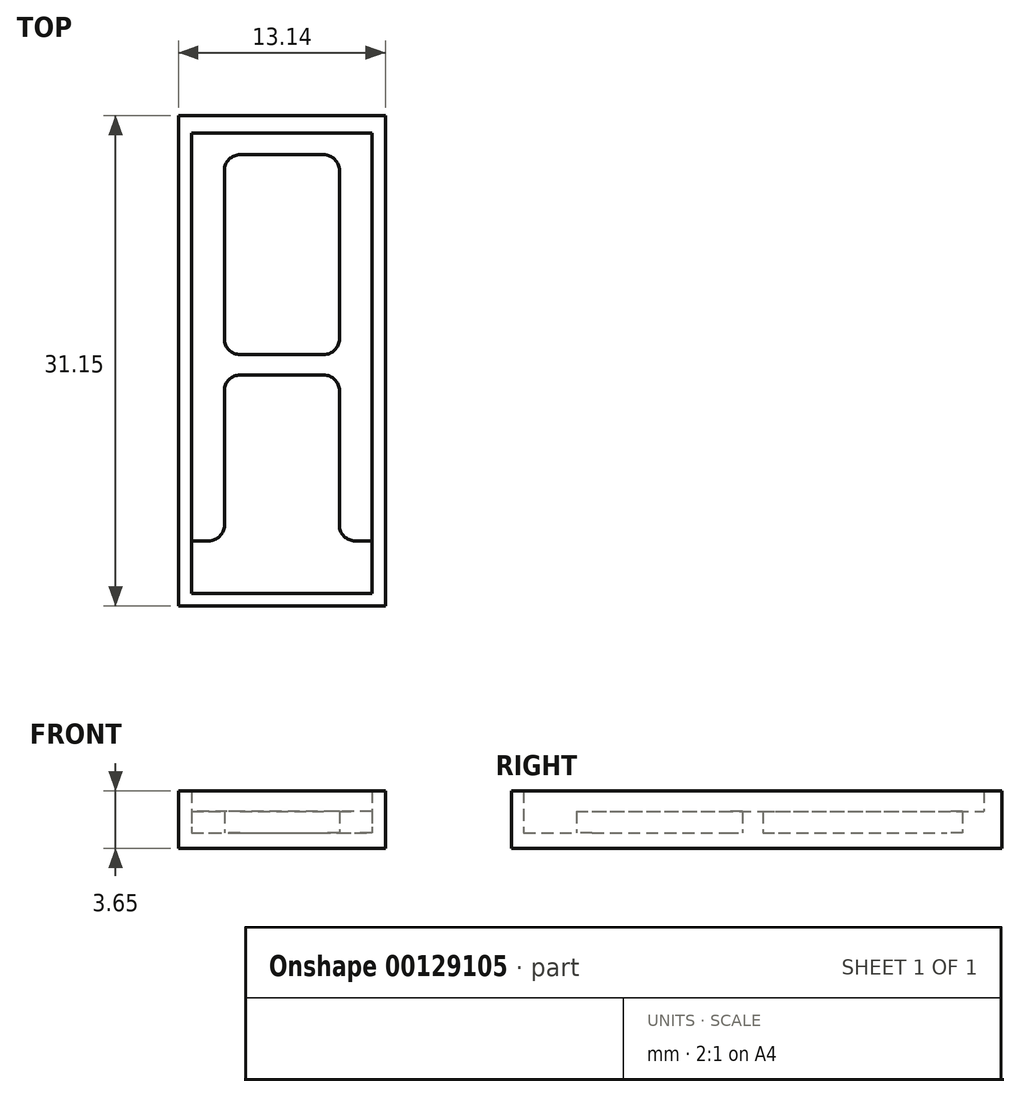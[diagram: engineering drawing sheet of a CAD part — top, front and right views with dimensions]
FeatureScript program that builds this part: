
annotation { "Feature Type Name" : "Feature", "Feature Type Description" : "" }
export const myFeature = defineFeature(function(context is Context, id is Id, definition is map)
    precondition{}
    {
        {
            var Q0;
            Q0=qCreatedBy(makeId("Top.planeOp"),FACE);
            var sketch = newSketch(context, id + "F0", { "sketchPlane" : qUnion([Q0])});
            skLineSegment(sketch, "E0", {"start": v(5.72, 5.55) * mm, "end": v(5.72, 34.8) * mm});
            skLineSegment(sketch, "E1", {"start": v(5.72, 8.9) * mm, "end": v(4.65, 8.9) * mm});
            skLineSegment(sketch, "E2", {"start": v(3.65, 9.9) * mm, "end": v(3.65, 18.44) * mm});
            skLineSegment(sketch, "E3", {"start": v(6.57, 35.92) * mm, "end": v(6.57, 4.77) * mm});
            skLineSegment(sketch, "E4", {"start": v(0, 0) * mm, "end": v(0, 51.69) * mm, "construction": true});
            skLineSegment(sketch, "E5", {"start": v(5.72, 5.55) * mm, "end": v(0, 5.55) * mm});
            skLineSegment(sketch, "E6", {"start": v(6.57, 4.77) * mm, "end": v(0, 4.77) * mm});
            skLineSegment(sketch, "E7", {"start": v(2.65, 33.43) * mm, "end": v(0, 33.43) * mm});
            skLineSegment(sketch, "E8", {"start": v(5.72, 34.8) * mm, "end": v(0, 34.8) * mm});
            skLineSegment(sketch, "E9", {"start": v(6.57, 35.92) * mm, "end": v(0, 35.92) * mm});
            skLineSegment(sketch, "E10.MirrorCS", {"start": v(-6.57, 4.77) * mm, "end": v(0, 4.77) * mm});
            skLineSegment(sketch, "E11.MirrorCS", {"start": v(-3.65, 9.9) * mm, "end": v(-3.65, 18.44) * mm});
            skLineSegment(sketch, "E12.MirrorCS", {"start": v(-5.72, 5.55) * mm, "end": v(-5.72, 34.8) * mm});
            skLineSegment(sketch, "E13.MirrorCS", {"start": v(-5.72, 8.9) * mm, "end": v(-4.65, 8.9) * mm});
            skLineSegment(sketch, "E14.MirrorCS", {"start": v(-6.57, 35.92) * mm, "end": v(-6.57, 4.77) * mm});
            skLineSegment(sketch, "E15.MirrorCS", {"start": v(-6.57, 35.92) * mm, "end": v(0, 35.92) * mm});
            skLineSegment(sketch, "E16.MirrorCS", {"start": v(-5.72, 34.8) * mm, "end": v(0, 34.8) * mm});
            skLineSegment(sketch, "E17.MirrorCS", {"start": v(-2.65, 33.43) * mm, "end": v(0, 33.43) * mm});
            skLineSegment(sketch, "E18.MirrorCS", {"start": v(-5.72, 5.55) * mm, "end": v(0, 5.55) * mm});
            skLineSegment(sketch, "E19", {"start": v(2.65, 20.74) * mm, "end": v(-2.65, 20.74) * mm});
            skLineSegment(sketch, "E20", {"start": v(-2.65, 19.44) * mm, "end": v(2.65, 19.44) * mm});
            skLineSegment(sketch, "E21.trimOffspring", {"start": v(-3.65, 21.74) * mm, "end": v(-3.65, 32.43) * mm});
            skLineSegment(sketch, "E22.trimOffspring", {"start": v(3.65, 21.74) * mm, "end": v(3.65, 32.43) * mm});
            skPoint(sketch, "E23.visualSharp", {"position": v(-3.65, 20.74) * mm});
            skArc(sketch, "E23.filletArc", {"start": v(-3.65, 21.74) * mm, "mid": v(-3.36, 21.03) * mm, "end": v(-2.65, 20.74) * mm});
            skPoint(sketch, "E24.visualSharp", {"position": v(3.65, 20.74) * mm});
            skArc(sketch, "E24.filletArc", {"start": v(2.65, 20.74) * mm, "mid": v(3.36, 21.03) * mm, "end": v(3.65, 21.74) * mm});
            skPoint(sketch, "E25.visualSharp", {"position": v(3.65, 33.43) * mm});
            skArc(sketch, "E25.filletArc", {"start": v(3.65, 32.43) * mm, "mid": v(3.36, 33.14) * mm, "end": v(2.65, 33.43) * mm});
            skPoint(sketch, "E26.visualSharp", {"position": v(-3.65, 33.43) * mm});
            skArc(sketch, "E26.filletArc", {"start": v(-2.65, 33.43) * mm, "mid": v(-3.36, 33.14) * mm, "end": v(-3.65, 32.43) * mm});
            skPoint(sketch, "E27.visualSharp", {"position": v(-3.65, 19.44) * mm});
            skArc(sketch, "E27.filletArc", {"start": v(-2.65, 19.44) * mm, "mid": v(-3.36, 19.14) * mm, "end": v(-3.65, 18.44) * mm});
            skPoint(sketch, "E28.visualSharp", {"position": v(3.65, 19.44) * mm});
            skArc(sketch, "E28.filletArc", {"start": v(3.65, 18.44) * mm, "mid": v(3.36, 19.14) * mm, "end": v(2.65, 19.44) * mm});
            skPoint(sketch, "E29.visualSharp", {"position": v(3.65, 8.9) * mm});
            skArc(sketch, "E29.filletArc", {"start": v(3.65, 9.9) * mm, "mid": v(3.94, 9.2) * mm, "end": v(4.65, 8.9) * mm});
            skPoint(sketch, "E30.visualSharp", {"position": v(-3.65, 8.9) * mm});
            skArc(sketch, "E30.filletArc", {"start": v(-4.65, 8.9) * mm, "mid": v(-3.94, 9.2) * mm, "end": v(-3.65, 9.9) * mm});
            skSolve(sketch);
        }
        {
            var Q0;
            {var subQ5=sQuery(id+"F0.wireOp",EDGE,"E1");Q0=makeQuery(id+"F0.imprint","IMPRINT",FACE,{"disambiguationData":[TD([[makeQuery(id+"F0.imprint","IMPRINT",EDGE,{"derivedFrom":subQ5}),1.0]])]});}
            var Q1;
            Q1=makeQuery(id+"F0.imprint","IMPRINT",FACE,{"disambiguationData":[TD([[makeQuery(id+"F0.imprint","IMPRINT",EDGE,{"derivedFrom":sQuery(id+"F0.wireOp",EDGE,"E7")}),1.0]])]});
            extrude(context, id + "F1", {"entities" : qUnion([Q0, Q1]), "depth" : 0.98 * mm});
        }
        {
            var Q0;
            {var subQ5=sQuery(id+"F0.wireOp",EDGE,"E1");Q0=makeQuery(id+"F0.imprint","IMPRINT",FACE,{"disambiguationData":[TD([[makeQuery(id+"F0.imprint","IMPRINT",EDGE,{"derivedFrom":subQ5}),-1.0]])]});}
            extrude(context, id + "F2", {"entities" : qUnion([Q0]), "operationType" : NewBodyOperationType.ADD, "depth" : 2.34 * mm});
        }
        {
            var Q0;
            Q0=makeQuery(id+"F0.imprint","IMPRINT",FACE,{"disambiguationData":[TD([[makeQuery(id+"F0.imprint","IMPRINT",EDGE,{"derivedFrom":sQuery(id+"F0.wireOp",EDGE,"E3")}),-1.0]])]});
            extrude(context, id + "F3", {"entities" : qUnion([Q0]), "operationType" : NewBodyOperationType.ADD, "depth" : 3.65 * mm});
        }
    });
